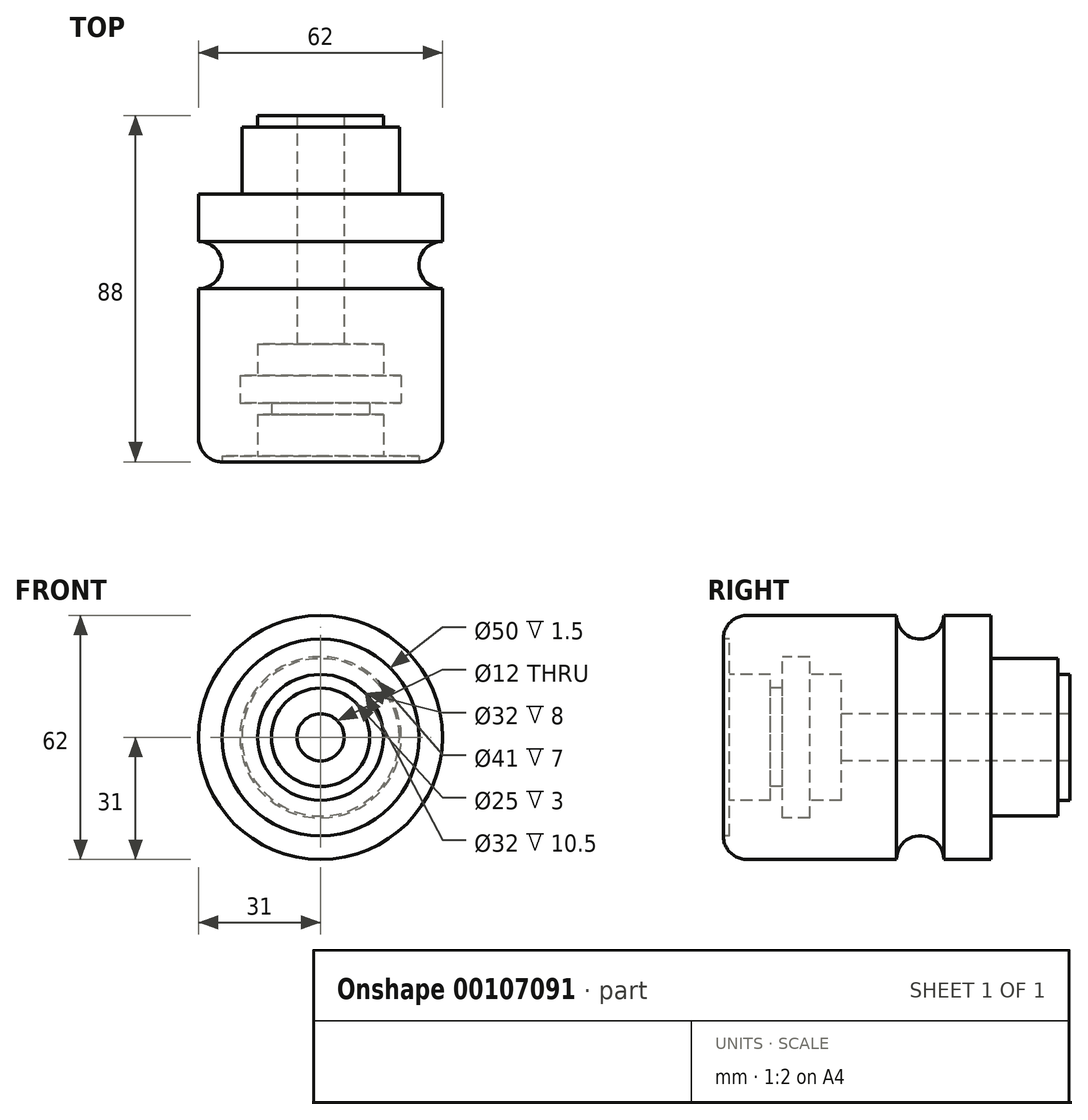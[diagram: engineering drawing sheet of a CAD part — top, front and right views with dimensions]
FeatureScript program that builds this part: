
annotation { "Feature Type Name" : "Feature", "Feature Type Description" : "" }
export const myFeature = defineFeature(function(context is Context, id is Id, definition is map)
    precondition{}
    {
        {
            var Q0;
            Q0=qCreatedBy(makeId("Right.planeOp"),FACE);
            var sketch = newSketch(context, id + "F0", { "sketchPlane" : qUnion([Q0])});
            skLineSegment(sketch, "E0", {"start": v(-8.3, 0) * mm, "end": v(44, 0) * mm, "construction": true});
            skLineSegment(sketch, "E1", {"start": v(0, 0) * mm, "end": v(0, 25) * mm});
            skLineSegment(sketch, "E2", {"start": v(6, 31) * mm, "end": v(44, 31) * mm});
            skLineSegment(sketch, "E3", {"start": v(44, 31) * mm, "end": v(44, 0) * mm});
            skLineSegment(sketch, "E4", {"start": v(56, 31) * mm, "end": v(56, 0) * mm});
            skLineSegment(sketch, "E5", {"start": v(56, 31) * mm, "end": v(68, 31) * mm});
            skLineSegment(sketch, "E6", {"start": v(68, 31) * mm, "end": v(68, 0) * mm});
            skLineSegment(sketch, "E7", {"start": v(68, 20) * mm, "end": v(85, 20) * mm});
            skLineSegment(sketch, "E8", {"start": v(85, 0) * mm, "end": v(85, 20) * mm});
            skLineSegment(sketch, "E9", {"start": v(85, 16) * mm, "end": v(88, 16) * mm});
            skLineSegment(sketch, "E10", {"start": v(88, 16) * mm, "end": v(88, 0) * mm});
            skArc(sketch, "E11", {"start": v(44, 31) * mm, "mid": v(50, 25) * mm, "end": v(56, 31) * mm});
            skLineSegment(sketch, "E12", {"start": v(0, 0) * mm, "end": v(88, 0) * mm});
            skPoint(sketch, "E13.visualSharp", {"position": v(0, 31) * mm});
            skArc(sketch, "E13.filletArc", {"start": v(6, 31) * mm, "mid": v(1.76, 29.24) * mm, "end": v(0, 25) * mm});
            skPoint(sketch, "E14.visualSharp", {"position": v(0, 0) * mm});
            skSolve(sketch);
        }
        {
            var Q0;
            Q0=makeQuery(id+"F0.imprint","IMPRINT",FACE,{"disambiguationData":[TD([[makeQuery(id+"F0.imprint","IMPRINT",EDGE,{"derivedFrom":sQuery(id+"F0.wireOp",EDGE,"E1")}),-1.0]])]});
            var Q1;
            {var subQ0=sQuery(id+"F0.wireOp",EDGE,"E3");Q1=makeQuery(id+"F0.imprint","IMPRINT",FACE,{"disambiguationData":[TD([[makeQuery(id+"F0.imprint","IMPRINT",EDGE,{"derivedFrom":subQ0}),1.0]])]});}
            var Q2;
            {var subQ5=sQuery(id+"F0.wireOp",EDGE,"E4");Q2=makeQuery(id+"F0.imprint","IMPRINT",FACE,{"disambiguationData":[TD([[makeQuery(id+"F0.imprint","IMPRINT",EDGE,{"derivedFrom":subQ5}),1.0]])]});}
            var Q3;
            {var subQ1=sQuery(id+"F0.wireOp",EDGE,"E7");Q3=makeQuery(id+"F0.imprint","IMPRINT",FACE,{"disambiguationData":[TD([[makeQuery(id+"F0.imprint","IMPRINT",EDGE,{"derivedFrom":subQ1}),-1.0]])]});}
            var Q4;
            {var subQ3=sQuery(id+"F0.wireOp",EDGE,"E9");Q4=makeQuery(id+"F0.imprint","IMPRINT",FACE,{"disambiguationData":[TD([[makeQuery(id+"F0.imprint","IMPRINT",EDGE,{"derivedFrom":subQ3}),-1.0]])]});}
            var Q5;
            Q5=sQuery(id+"F0.wireOp",EDGE,"E0");
            revolve(context, id + "F1", {"entities" : qUnion([Q0, Q1, Q2, Q3, Q4]), "axis" : qUnion([Q5]), "revolveType" : RevolveType.FULL});
        }
        {
            var Q0;
            Q0=qCreatedBy(makeId("Right.planeOp"),FACE);
            var sketch = newSketch(context, id + "F2", { "sketchPlane" : qUnion([Q0])});
            skLineSegment(sketch, "E15", {"start": v(0, 0) * mm, "end": v(0, 25) * mm});
            skLineSegment(sketch, "E16", {"start": v(0, 25) * mm, "end": v(1.5, 25) * mm});
            skLineSegment(sketch, "E17", {"start": v(1.5, 25) * mm, "end": v(1.5, 16) * mm});
            skLineSegment(sketch, "E18", {"start": v(1.5, 16) * mm, "end": v(12, 16) * mm});
            skLineSegment(sketch, "E19", {"start": v(12, 16) * mm, "end": v(12, 12.5) * mm});
            skLineSegment(sketch, "E20", {"start": v(12, 12.5) * mm, "end": v(15, 12.5) * mm});
            skLineSegment(sketch, "E21", {"start": v(15, 12.5) * mm, "end": v(15, 20.5) * mm});
            skLineSegment(sketch, "E22", {"start": v(15, 20.5) * mm, "end": v(22, 20.5) * mm});
            skLineSegment(sketch, "E23", {"start": v(22, 20.5) * mm, "end": v(22, 16) * mm});
            skLineSegment(sketch, "E24", {"start": v(30, 6) * mm, "end": v(88, 6) * mm});
            skLineSegment(sketch, "E25", {"start": v(88, 6) * mm, "end": v(88, 0) * mm});
            skLineSegment(sketch, "E26", {"start": v(30, 6) * mm, "end": v(30, 16) * mm});
            skLineSegment(sketch, "E27", {"start": v(30, 16) * mm, "end": v(22, 16) * mm});
            skLineSegment(sketch, "E28", {"start": v(88, 0) * mm, "end": v(0, 0) * mm});
            skPoint(sketch, "E29.orphan", {"position": v(1.5, 0) * mm});
            skLineSegment(sketch, "E30", {"start": v(-21.45, 0) * mm, "end": v(91.7, 0) * mm, "construction": true});
            skSolve(sketch);
        }
        {
            var Q0;
            Q0=makeQuery(id+"F2.imprint","IMPRINT",FACE,{"disambiguationData":[TD([[makeQuery(id+"F2.imprint","IMPRINT",EDGE,{"derivedFrom":sQuery(id+"F2.wireOp",EDGE,"E15")}),-1.0]])]});
            var Q1;
            Q1=sQuery(id+"F2.wireOp",EDGE,"E30");
            revolve(context, id + "F3", {"operationType" : NewBodyOperationType.REMOVE, "entities" : qUnion([Q0]), "axis" : qUnion([Q1]), "revolveType" : RevolveType.FULL});
        }
    });
